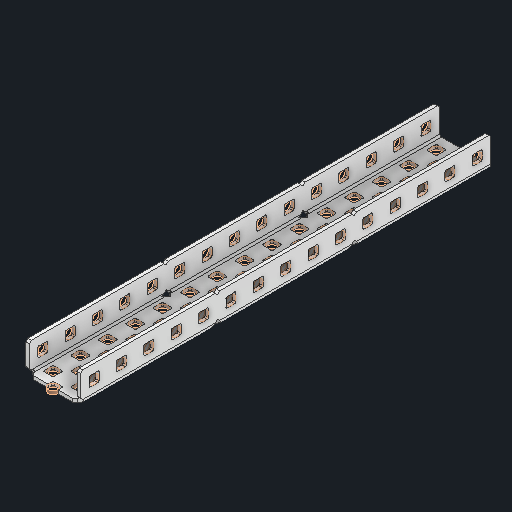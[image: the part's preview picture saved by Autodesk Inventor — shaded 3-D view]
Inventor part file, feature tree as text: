
AUTODESK INVENTOR PART (.ipt)
format: ipt  version: 2024 (Build 280153000, 153)  size: 1,321,472 bytes
history: native  units: in
note: dims shown in document units (in); Inventor stores cm internally (conversion verified against a paired STEP export)
features: other x156, sketch x5, sheet_metal_op x1
ambient origin geometry x8: Origin, YZ Plane, XZ Plane, XY Plane, X Axis, Y Axis, Z Axis, Center Point
bodies: Solid1 (feature_tree)
feature tree (162):
  other  "Alu C 1x2x1x15.ipt"
  other  "Solid1::Alu C 1x2x1x15.ipt"
  other  "TaggingFeature1"
  sketch  "Sketch1"  dims[d0=0.3937in]
  sketch  "Sketch2"  dims[d1=0.0625in]
  sketch  "Sketch3"
  other  "Flange Pattern Sketch"
  sketch  "Sketch9"
  sheet_metal_op  "Body Pattern Sketch"
  other  "Arc Length"
  sketch  "Sketch14"
  other  "Flange Pattern Plane"
  other  "Srf1"
  other  "Srf2"
  other  "Srf3"
  other  "Srf4"
  other  "Srf5"
  other  "Srf6"
  other  "Srf7"
  other  "Srf8"
  other  "Srf9"
  other  "Srf10"
  other  "Srf11"
  other  "Srf12"
  other  "Srf13"
  other  "Srf14"
  other  "Srf15"
  other  "Srf16"
  other  "Srf17"
  other  "Srf18"
  other  "Srf19"
  other  "Srf20"
  other  "Srf21"
  other  "Srf22"
  other  "Srf23"
  other  "Srf24"
  other  "Srf25"
  other  "Srf26"
  other  "Srf27"
  other  "Srf28"
  other  "Srf29"
  other  "Srf30"
  other  "Srf31"
  other  "Srf32"
  other  "Srf33"
  other  "Srf34"
  other  "Srf35"
  other  "Srf36"
  other  "Srf37"
  other  "Srf38"
  other  "Srf39"
  other  "Srf40"
  other  "Srf41"
  other  "Srf42"
  other  "Srf43"
  other  "Srf44"
  other  "Srf45"
  other  "Srf46"
  other  "Srf47"
  other  "Srf48"
  other  "Srf49"
  other  "Srf50"
  other  "Srf51"
  other  "Srf52"
  other  "Srf53"
  other  "Srf54"
  other  "Srf55"
  other  "Srf56"
  other  "Srf57"
  other  "Srf58"
  other  "Srf59"
  other  "Srf60"
  other  "Srf61"
  other  "Srf62"
  other  "Srf63"
  other  "Srf64"
  other  "Srf65"
  other  "Srf66"
  other  "Srf67"
  other  "Srf68"
  other  "Srf69"
  other  "Srf70"
  other  "Srf71"
  other  "Srf72"
  other  "Srf73"
  other  "Srf74"
  other  "Srf75"
  other  "Srf1::Derived"
  other  "Srf2::Derived"
  other  "Srf823::Derived"
  other  "Srf824::Derived"
  other  "Srf825::Derived"
  other  "Srf826::Derived"
  other  "Srf827::Derived"
  other  "Srf828::Derived"
  other  "Srf829::Derived"
  other  "Srf922::Derived"
  other  "Srf923::Derived"
  other  "Srf924::Derived"
  other  "Srf925::Derived"
  other  "Srf926::Derived"
  other  "Srf1143::Derived"
  other  "Srf1144::Derived"
  other  "Srf1145::Derived"
  other  "Srf1146::Derived"
  other  "Srf1147::Derived"
  other  "Srf1148::Derived"
  other  "Srf1149::Derived"
  other  "Srf1150::Derived"
  other  "Srf1151::Derived"
  other  "Srf1152::Derived"
  other  "Srf1153::Derived"
  other  "Srf1154::Derived"
  other  "Srf1155::Derived"
  other  "Srf1156::Derived"
  other  "Srf1157::Derived"
  other  "Srf1158::Derived"
  other  "Srf91::Derived"
  other  "Srf92::Derived"
  other  "Srf856::Derived"
  other  "Srf857::Derived"
  other  "Srf858::Derived"
  other  "Srf859::Derived"
  other  "Srf860::Derived"
  other  "Srf861::Derived"
  other  "Srf862::Derived"
  other  "Srf959::Derived"
  other  "Srf960::Derived"
  other  "Srf961::Derived"
  other  "Srf962::Derived"
  other  "Srf963::Derived"
  other  "Srf1199::Derived"
  other  "Srf1200::Derived"
  other  "Srf1201::Derived"
  other  "Srf1202::Derived"
  other  "Srf1203::Derived"
  other  "Srf1204::Derived"
  other  "Srf1205::Derived"
  other  "Srf1206::Derived"
  other  "Srf1207::Derived"
  other  "Srf1208::Derived"
  other  "Srf1209::Derived"
  other  "Srf1210::Derived"
  other  "Srf1211::Derived"
  other  "Srf1212::Derived"
  other  "Srf1213::Derived"
  other  "Srf1214::Derived"
  other  "Srf786::Derived"
  other  "Srf889::Derived"
  other  "Srf890::Derived"
  other  "Srf891::Derived"
  other  "Srf892::Derived"
  other  "Srf893::Derived"
  other  "Srf894::Derived"
  other  "Srf895::Derived"
  other  "Srf896::Derived"
  other  "Srf996::Derived"
  other  "Srf997::Derived"
  other  "Srf998::Derived"
  other  "Srf999::Derived"
  other  "Srf1000::Derived"
  other  "Srf1255::Derived"
